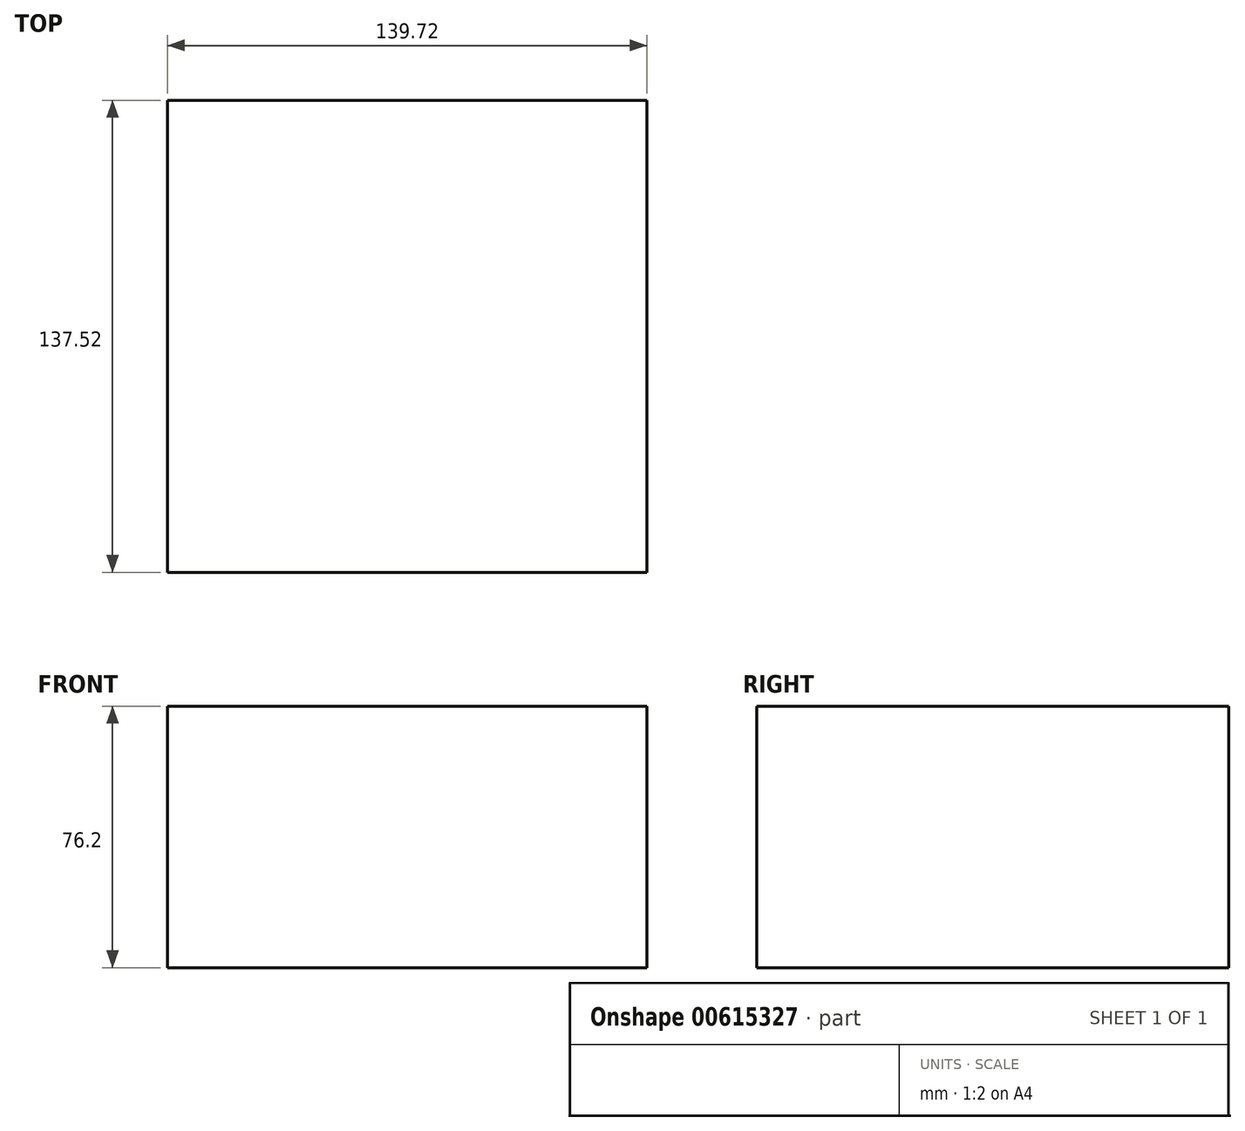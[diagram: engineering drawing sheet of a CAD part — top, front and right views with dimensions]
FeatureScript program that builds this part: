
annotation { "Feature Type Name" : "Feature", "Feature Type Description" : "" }
export const myFeature = defineFeature(function(context is Context, id is Id, definition is map)
    precondition{}
    {
        {
            var Q0;
            Q0=qCreatedBy(makeId("Top.planeOp"),FACE);
            var sketch = newSketch(context, id + "F0", { "sketchPlane" : qUnion([Q0])});
            skLineSegment(sketch, "E0.bottom", {"start": v(69.86, -68.76) * mm, "end": v(-69.86, -68.76) * mm});
            skLineSegment(sketch, "E0.top", {"start": v(69.86, 68.76) * mm, "end": v(-69.86, 68.76) * mm});
            skLineSegment(sketch, "E0.left", {"start": v(69.86, -68.76) * mm, "end": v(69.86, 68.76) * mm});
            skLineSegment(sketch, "E0.right", {"start": v(-69.86, -68.76) * mm, "end": v(-69.86, 68.76) * mm});
            skPoint(sketch, "E0.middle", {"position": v(0, 0) * mm});
            skLineSegment(sketch, "E1", {"start": v(0, 68.76) * mm, "end": v(0, -68.76) * mm});
            skSolve(sketch);
        }
        {
            var Q0;
            Q0=qCreatedBy(makeId("Top.planeOp"),FACE);
            var sketch = newSketch(context, id + "F1", { "sketchPlane" : qUnion([Q0])});
            skCircle(sketch, "E2", {"center": v(54.26, 0) * mm, "radius": 9.82 * mm});
            skSolve(sketch);
        }
        {
            var Q0;
            {var subQ0=sQuery(id+"F0.wireOp",EDGE,"E0.right");Q0=makeQuery(id+"F0.imprint","IMPRINT",FACE,{"disambiguationData":[TD([[makeQuery(id+"F0.imprint","IMPRINT",EDGE,{"derivedFrom":subQ0}),-1.0]])]});}
            extrude(context, id + "F2", {"entities" : qUnion([Q0]), "oppositeDirection" : true, "depth" : 25.4 * mm, "offsetDistance" : 25.4 * mm});
        }
        {
            var Q0;
            {var subQ0=sQuery(id+"F0.wireOp",EDGE,"E0.left");Q0=makeQuery(id+"F0.imprint","IMPRINT",FACE,{"disambiguationData":[TD([[makeQuery(id+"F0.imprint","IMPRINT",EDGE,{"derivedFrom":subQ0}),1.0]])]});}
            var Q1;
            {var subQ0=sQuery(id+"F0.wireOp",EDGE,"E0.right");Q1=makeQuery(id+"F0.imprint","IMPRINT",FACE,{"disambiguationData":[TD([[makeQuery(id+"F0.imprint","IMPRINT",EDGE,{"derivedFrom":subQ0}),-1.0]])]});}
            extrude(context, id + "F3", {"entities" : qUnion([Q0, Q1]), "operationType" : NewBodyOperationType.ADD, "oppositeDirection" : true, "depth" : 76.2 * mm, "offsetDistance" : 25.4 * mm});
        }
        {
            var Q0;
            Q0=sQuery(id+"F1.wireOp",EDGE,"E2");
            var Q1;
            Q1=sQuery(id+"F0.wireOp",EDGE,"E1");
            revolve(context, id + "F4", {"bodyType" : ToolBodyType.SURFACE, "surfaceEntities" : qUnion([Q0]), "axis" : qUnion([Q1]), "revolveType" : RevolveType.FULL});
        }
    });
